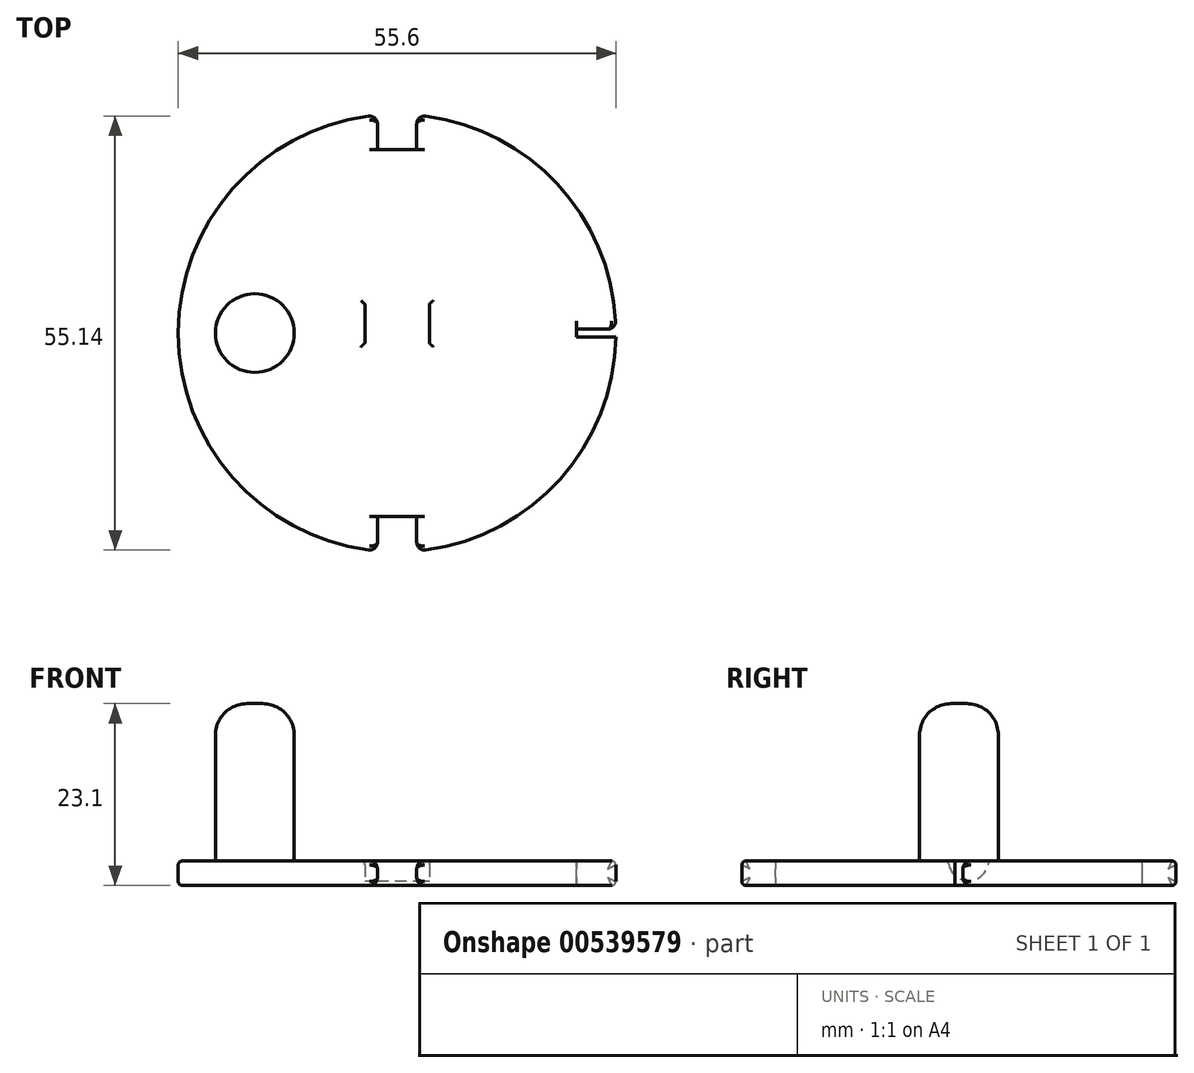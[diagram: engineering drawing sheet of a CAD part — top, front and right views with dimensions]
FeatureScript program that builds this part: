
annotation { "Feature Type Name" : "Feature", "Feature Type Description" : "" }
export const myFeature = defineFeature(function(context is Context, id is Id, definition is map)
    precondition{}
    {
        {
            var Q0;
            Q0=qCreatedBy(makeId("Top.planeOp"),FACE);
            var sketch = newSketch(context, id + "F0", { "sketchPlane" : qUnion([Q0])});
            skCircle(sketch, "E0", {"center": v(0, 0) * mm, "radius": 27.8 * mm});
            skSolve(sketch);
        }
        {
            var Q0;
            Q0=qSketchRegion(id+"F0",true);
            extrude(context, id + "F1", {"entities" : qUnion([Q0]), "depth" : 3.1 * mm});
        }
        {
            var Q0;
            Q0=makeQuery(id+"F1.opExtrude","CAP_FACE",FACE,{"disambiguationData":[OSD([sQuery(id+"F0.wireOp",EDGE,"E0")])],"isStart":false});
            var Q1;
            Q1=makeQuery(id+"F1.opExtrude","CAP_FACE",FACE,{"disambiguationData":[OSD([sQuery(id+"F0.wireOp",EDGE,"E0")])],"isStart":true});
            fillet(context, id + "F2", {"entities" : qUnion([Q0, Q1]), "radius" : 0.5 * mm, "tangentPropagation" : true, "allowEdgeOverflow" : false});
        }
        {
            var Q0;
            Q0=makeQuery(id+"F1.opExtrude","CAP_FACE",FACE,{"disambiguationData":[OSD([sQuery(id+"F0.wireOp",EDGE,"E0")])],"isStart":false});
            var sketch = newSketch(context, id + "F3", { "sketchPlane" : qUnion([Q0])});
            skLineSegment(sketch, "E1.bottom", {"start": v(-2.5, 28.3) * mm, "end": v(2.5, 28.3) * mm});
            skLineSegment(sketch, "E1.top", {"start": v(-2.5, 23.3) * mm, "end": v(2.5, 23.3) * mm});
            skLineSegment(sketch, "E1.left", {"start": v(-2.5, 28.3) * mm, "end": v(-2.5, 23.3) * mm});
            skLineSegment(sketch, "E1.right", {"start": v(2.5, 28.3) * mm, "end": v(2.5, 23.3) * mm});
            skPoint(sketch, "E1.middle", {"position": v(0, 25.8) * mm});
            skLineSegment(sketch, "E2.MirrorCS", {"start": v(-2.5, -23.3) * mm, "end": v(2.5, -23.3) * mm});
            skLineSegment(sketch, "E3.MirrorCS", {"start": v(-2.5, -28.3) * mm, "end": v(2.5, -28.3) * mm});
            skLineSegment(sketch, "E4.MirrorCS", {"start": v(-2.5, -28.3) * mm, "end": v(-2.5, -23.3) * mm});
            skPoint(sketch, "E5.MirrorP", {"position": v(0, -25.8) * mm});
            skLineSegment(sketch, "E6.MirrorCS", {"start": v(2.5, -28.3) * mm, "end": v(2.5, -23.3) * mm});
            skSolve(sketch);
        }
        {
            var Q0;
            Q0=qSketchRegion(id+"F3",true);
            extrude(context, id + "F4", {"entities" : qUnion([Q0]), "operationType" : NewBodyOperationType.REMOVE, "endBound" : BoundingType.THROUGH_ALL, "oppositeDirection" : true, "depth" : 25 * mm, "offsetDistance" : 25 * mm});
        }
        {
            var Q0;
            Q0=makeQuery(id+"F4.boolean.opBoolean","INTERSECT",EDGE,{"derivedFrom":[makeQuery(id+"F1.opExtrude","SWEPT_FACE",FACE,{"disambiguationData":[OSD([sQuery(id+"F0.wireOp",EDGE,"E0")])]}),makeQuery(id+"F4.opExtrude","SWEPT_FACE",FACE,{"disambiguationData":[OSD([sQuery(id+"F3.wireOp",EDGE,"E4.MirrorCS")])]})]});
            var Q1;
            Q1=makeQuery(id+"F4.boolean.opBoolean","INTERSECT",EDGE,{"derivedFrom":[makeQuery(id+"F1.opExtrude","SWEPT_FACE",FACE,{"disambiguationData":[OSD([sQuery(id+"F0.wireOp",EDGE,"E0")])]}),makeQuery(id+"F4.opExtrude","SWEPT_FACE",FACE,{"disambiguationData":[OSD([sQuery(id+"F3.wireOp",EDGE,"E6.MirrorCS")])]})]});
            var Q2;
            Q2=makeQuery(id+"F4.boolean.opBoolean","INTERSECT",EDGE,{"derivedFrom":[makeQuery(id+"F1.opExtrude","SWEPT_FACE",FACE,{"disambiguationData":[OSD([sQuery(id+"F0.wireOp",EDGE,"E0")])]}),makeQuery(id+"F4.opExtrude","SWEPT_FACE",FACE,{"disambiguationData":[OSD([sQuery(id+"F3.wireOp",EDGE,"E1.left")])]})]});
            var Q3;
            Q3=makeQuery(id+"F4.boolean.opBoolean","INTERSECT",EDGE,{"derivedFrom":[makeQuery(id+"F1.opExtrude","SWEPT_FACE",FACE,{"disambiguationData":[OSD([sQuery(id+"F0.wireOp",EDGE,"E0")])]}),makeQuery(id+"F4.opExtrude","SWEPT_FACE",FACE,{"disambiguationData":[OSD([sQuery(id+"F3.wireOp",EDGE,"E1.right")])]})]});
            fillet(context, id + "F5", {"entities" : qUnion([Q0, Q1, Q2, Q3]), "radius" : 1 * mm, "tangentPropagation" : true, "allowEdgeOverflow" : false});
        }
        {
            var Q0;
            Q0=makeQuery(id+"F1.opExtrude","CAP_FACE",FACE,{"disambiguationData":[OSD([sQuery(id+"F0.wireOp",EDGE,"E0")])],"isStart":false});
            var sketch = newSketch(context, id + "F6", { "sketchPlane" : qUnion([Q0])});
            skCircle(sketch, "E7", {"center": v(-18.07, 0) * mm, "radius": 5 * mm});
            skSolve(sketch);
        }
        {
            var Q0;
            Q0=qSketchRegion(id+"F6",true);
            extrude(context, id + "F7", {"entities" : qUnion([Q0]), "operationType" : NewBodyOperationType.ADD, "depth" : 20 * mm, "offsetDistance" : 25 * mm});
        }
        {
            var Q0;
            Q0=makeQuery(id+"F7.opExtrude","CAP_FACE",FACE,{"disambiguationData":[OSD([sQuery(id+"F6.wireOp",EDGE,"E7")])],"isStart":false});
            var Q1;
            Q1=makeQuery(id+"F7.opExtrude","CAP_EDGE",EDGE,{"disambiguationData":[OSD([sQuery(id+"F6.wireOp",EDGE,"E7")])],"isStart":true});
            fillet(context, id + "F8", {"entities" : qUnion([Q0, Q1]), "radius" : 4 * mm, "tangentPropagation" : true, "allowEdgeOverflow" : false});
        }
        {
            var Q0;
            Q0=makeQuery(id+"F1.opExtrude","CAP_FACE",FACE,{"disambiguationData":[OSD([sQuery(id+"F0.wireOp",EDGE,"E0")])],"isStart":false});
            var sketch = newSketch(context, id + "F9", { "sketchPlane" : qUnion([Q0])});
            skLineSegment(sketch, "E8.bottom", {"start": v(27.8, -0.5) * mm, "end": v(22.8, -0.5) * mm});
            skLineSegment(sketch, "E8.top", {"start": v(27.8, 0.5) * mm, "end": v(22.8, 0.5) * mm});
            skLineSegment(sketch, "E8.left", {"start": v(27.8, -0.5) * mm, "end": v(27.8, 0.5) * mm});
            skLineSegment(sketch, "E8.right", {"start": v(22.8, -0.5) * mm, "end": v(22.8, 0.5) * mm});
            skPoint(sketch, "E8.middle", {"position": v(25.3, 0) * mm});
            skPoint(sketch, "E8.middle.positionSnap0", {"position": v(27.3, 0) * mm});
            skPoint(sketch, "E8.centerSnap0", {"position": v(27.3, 0) * mm});
            skSolve(sketch);
        }
        {
            var Q0;
            {var subQ0=sQuery(id+"F9.wireOp",EDGE,"E8.right");Q0=makeQuery(id+"F9.imprint","IMPRINT",FACE,{"disambiguationData":[TD([[makeQuery(id+"F9.imprint","IMPRINT",EDGE,{"derivedFrom":subQ0}),-1.0]])]});}
            var Q1;
            Q1=qSketchRegion(id+"F9",true);
            extrude(context, id + "F10", {"entities" : qUnion([Q0, Q1]), "operationType" : NewBodyOperationType.REMOVE, "endBound" : BoundingType.THROUGH_ALL, "oppositeDirection" : true, "depth" : 25 * mm, "offsetDistance" : 25 * mm});
        }
        {
            var Q0;
            Q0=makeQuery(id+"F10.boolean.opBoolean","COPY",EDGE,{"derivedFrom":makeQuery(id+"F10.opExtrude","SWEPT_EDGE",EDGE,{"disambiguationData":[OSD([sQuery(id+"F9.wireOp",EDGE,"E8.top"),sQuery(id+"F9.wireOp",EDGE,"E8.left")])]})});
            var Q1;
            Q1=makeQuery(id+"F10.boolean.opBoolean","COPY",EDGE,{"derivedFrom":makeQuery(id+"F10.opExtrude","SWEPT_EDGE",EDGE,{"disambiguationData":[OSD([sQuery(id+"F9.wireOp",EDGE,"E8.bottom"),sQuery(id+"F9.wireOp",EDGE,"E8.left")])]})});
            fillet(context, id + "F11", {"entities" : qUnion([Q0, Q1]), "radius" : 1 * mm, "tangentPropagation" : true, "allowEdgeOverflow" : false});
        }
        {
            var Q0;
            Q0=qCreatedBy(makeId("Right.planeOp"),FACE);
            var sketch = newSketch(context, id + "F12", { "sketchPlane" : qUnion([Q0])});
            skCircle(sketch, "E9", {"center": v(1.2, 3.1) * mm, "radius": 2.5 * mm});
            skSolve(sketch);
        }
        {
            var Q0;
            Q0=qSketchRegion(id+"F12",true);
            extrude(context, id + "F13", {"entities" : qUnion([Q0]), "operationType" : NewBodyOperationType.REMOVE, "oppositeDirection" : true, "depth" : 4.1 * mm, "offsetDistance" : 25 * mm, "hasSecondDirection" : true, "secondDirectionOppositeDirection" : false, "secondDirectionDepth" : 4.1 * mm});
        }
        {
            var Q0;
            Q0=makeQuery(id+"F13.boolean.opBoolean","INTERSECT",EDGE,{"derivedFrom":[makeQuery(id+"F1.opExtrude","CAP_FACE",FACE,{"disambiguationData":[OSD([sQuery(id+"F0.wireOp",EDGE,"E0")])],"isStart":false}),makeQuery(id+"F13.opExtrude","CAP_FACE",FACE,{"disambiguationData":[OSD([sQuery(id+"F12.wireOp",EDGE,"E9")])],"isStart":true})]});
            var Q1;
            Q1=makeQuery(id+"F13.boolean.opBoolean","INTERSECT",EDGE,{"disambiguationData":[OD(0.0)],"derivedFrom":[makeQuery(id+"F1.opExtrude","CAP_FACE",FACE,{"disambiguationData":[OSD([sQuery(id+"F0.wireOp",EDGE,"E0")])],"isStart":false}),makeQuery(id+"F13.opExtrude","SWEPT_FACE",FACE,{"disambiguationData":[OSD([sQuery(id+"F12.wireOp",EDGE,"E9")])]})]});
            var Q2;
            Q2=makeQuery(id+"F13.boolean.opBoolean","INTERSECT",EDGE,{"disambiguationData":[OD(1.0)],"derivedFrom":[makeQuery(id+"F1.opExtrude","CAP_FACE",FACE,{"disambiguationData":[OSD([sQuery(id+"F0.wireOp",EDGE,"E0")])],"isStart":false}),makeQuery(id+"F13.opExtrude","SWEPT_FACE",FACE,{"disambiguationData":[OSD([sQuery(id+"F12.wireOp",EDGE,"E9")])]})]});
            var Q3;
            Q3=makeQuery(id+"F13.boolean.opBoolean","INTERSECT",EDGE,{"derivedFrom":[makeQuery(id+"F1.opExtrude","CAP_FACE",FACE,{"disambiguationData":[OSD([sQuery(id+"F0.wireOp",EDGE,"E0")])],"isStart":false}),makeQuery(id+"F13.opExtrude","CAP_FACE",FACE,{"disambiguationData":[OSD([sQuery(id+"F12.wireOp",EDGE,"E9")])],"isStart":false})]});
            fillet(context, id + "F14", {"entities" : qUnion([Q0, Q1, Q2, Q3]), "radius" : 0.5 * mm, "tangentPropagation" : true, "allowEdgeOverflow" : false});
        }
    });
